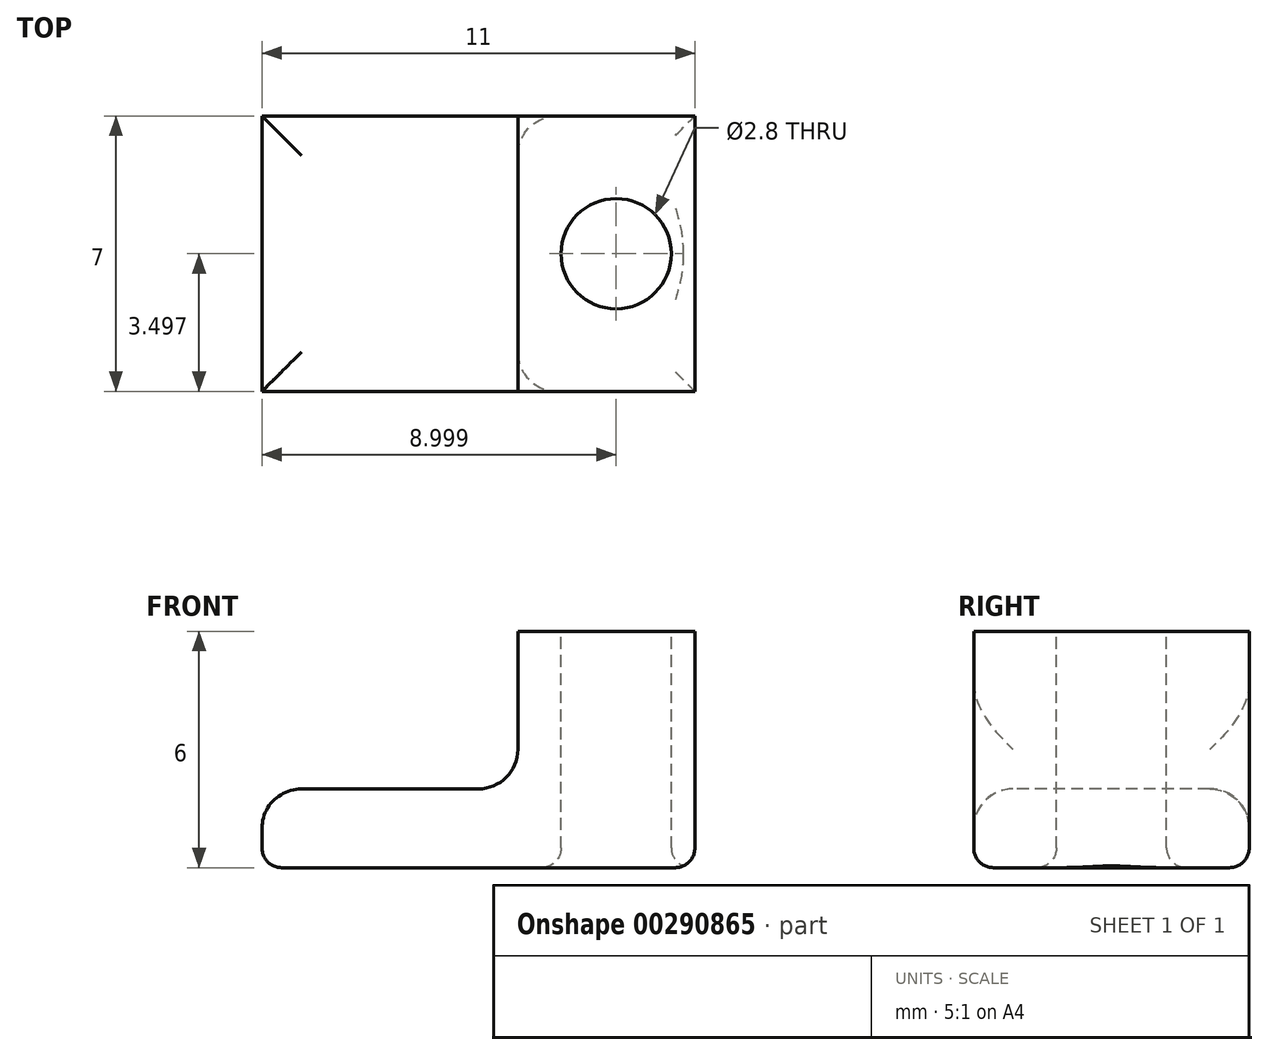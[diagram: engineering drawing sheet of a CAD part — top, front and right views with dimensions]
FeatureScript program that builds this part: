
annotation { "Feature Type Name" : "Feature", "Feature Type Description" : "" }
export const myFeature = defineFeature(function(context is Context, id is Id, definition is map)
    precondition{}
    {
        {
            var Q0;
            Q0=qCreatedBy(makeId("Top.planeOp"),FACE);
            var sketch = newSketch(context, id + "F0", { "sketchPlane" : qUnion([Q0])});
            skLineSegment(sketch, "E0.bottom", {"start": v(-8.23, 4.49) * mm, "end": v(4.27, 4.49) * mm});
            skLineSegment(sketch, "E0.top", {"start": v(-8.23, -2.51) * mm, "end": v(4.27, -2.51) * mm});
            skLineSegment(sketch, "E0.left", {"start": v(-8.23, 4.49) * mm, "end": v(-8.23, -2.51) * mm});
            skLineSegment(sketch, "E1.bottom", {"start": v(-8.23, 4.49) * mm, "end": v(-6.73, 4.49) * mm});
            skLineSegment(sketch, "E1.top", {"start": v(-8.23, -2.51) * mm, "end": v(-6.73, -2.51) * mm});
            skLineSegment(sketch, "E1.right", {"start": v(-6.73, 4.49) * mm, "end": v(-6.73, -2.51) * mm});
            skLineSegment(sketch, "E2", {"start": v(4.27, 4.49) * mm, "end": v(4.27, -2.51) * mm});
            skLineSegment(sketch, "E3.left", {"start": v(-0.23, 4.49) * mm, "end": v(-0.23, -2.51) * mm});
            skCircle(sketch, "E4", {"center": v(2.27, 0.99) * mm, "radius": 1.4 * mm});
            skSolve(sketch);
        }
        {
            var Q0;
            Q0=makeQuery(id+"F0.imprint","IMPRINT",FACE,{"disambiguationData":[TD([[makeQuery(id+"F0.imprint","IMPRINT",EDGE,{"derivedFrom":sQuery(id+"F0.wireOp",EDGE,"E1.bottom")}),-1.0]])]});
            var Q1;
            {var subQ0=sQuery(id+"F0.wireOp",EDGE,"E1.right");Q1=makeQuery(id+"F0.imprint","IMPRINT",FACE,{"disambiguationData":[TD([[makeQuery(id+"F0.imprint","IMPRINT",EDGE,{"derivedFrom":subQ0}),1.0]])]});}
            var Q2;
            {var subQ1=sQuery(id+"F0.wireOp",EDGE,"E2");Q2=makeQuery(id+"F0.imprint","IMPRINT",FACE,{"disambiguationData":[TD([[makeQuery(id+"F0.imprint","IMPRINT",EDGE,{"derivedFrom":subQ1}),-1.0]])]});}
            extrude(context, id + "F1", {"entities" : qUnion([Q0, Q1, Q2]), "oppositeDirection" : true, "depth" : 2 * mm});
        }
        {
            var Q0;
            Q0=makeQuery(id+"F0.imprint","IMPRINT",FACE,{"disambiguationData":[TD([[makeQuery(id+"F0.imprint","IMPRINT",EDGE,{"derivedFrom":sQuery(id+"F0.wireOp",EDGE,"E1.bottom")}),-1.0]])]});
            var Q1;
            {var subQ1=sQuery(id+"F0.wireOp",EDGE,"E2");Q1=makeQuery(id+"F0.imprint","IMPRINT",FACE,{"disambiguationData":[TD([[makeQuery(id+"F0.imprint","IMPRINT",EDGE,{"derivedFrom":subQ1}),-1.0]])]});}
            extrude(context, id + "F2", {"entities" : qUnion([Q0, Q1]), "operationType" : NewBodyOperationType.ADD, "depth" : 4 * mm});
        }
        {
            var Q0;
            Q0=makeQuery(id+"F1.opExtrude","CAP_FACE",FACE,{"disambiguationData":[OSD([sQuery(id+"F0.wireOp",EDGE,"E0.bottom"),sQuery(id+"F0.wireOp",EDGE,"E0.top"),sQuery(id+"F0.wireOp",EDGE,"E1.bottom"),sQuery(id+"F0.wireOp",EDGE,"E1.top"),sQuery(id+"F0.wireOp",EDGE,"E0.left"),sQuery(id+"F0.wireOp",EDGE,"E2"),sQuery(id+"F0.wireOp",EDGE,"E4")])],"isStart":true});
            var Q1;
            Q1=makeQuery(id+"F2.opExtrude","SWEPT_FACE",FACE,{"disambiguationData":[OSD([sQuery(id+"F0.wireOp",EDGE,"E1.right")])]});
            fillet(context, id + "F3", {"entities" : qUnion([Q0, Q1]), "radius" : 1 * mm, "tangentPropagation" : true, "allowEdgeOverflow" : false});
        }
        {
            var Q0;
            Q0=makeQuery(id+"F1.opExtrude","CAP_FACE",FACE,{"disambiguationData":[OSD([sQuery(id+"F0.wireOp",EDGE,"E0.bottom"),sQuery(id+"F0.wireOp",EDGE,"E0.top"),sQuery(id+"F0.wireOp",EDGE,"E1.bottom"),sQuery(id+"F0.wireOp",EDGE,"E1.top"),sQuery(id+"F0.wireOp",EDGE,"E0.left"),sQuery(id+"F0.wireOp",EDGE,"E2"),sQuery(id+"F0.wireOp",EDGE,"E4")])],"isStart":false});
            var Q1;
            {var subQ0=sQuery(id+"F0.wireOp",EDGE,"E0.left");Q1=makeQuery(id+"F2.boolean.opBoolean","MERGE",FACE,{"derivedFrom":[makeQuery(id+"F1.opExtrude","SWEPT_FACE",FACE,{"disambiguationData":[OSD([subQ0])]}),makeQuery(id+"F2.opExtrude","SWEPT_FACE",FACE,{"disambiguationData":[OSD([subQ0])]})]});}
            fillet(context, id + "F4", {"entities" : qUnion([Q0, Q1]), "radius" : 0.5 * mm, "tangentPropagation" : true, "allowEdgeOverflow" : false});
        }
    });
